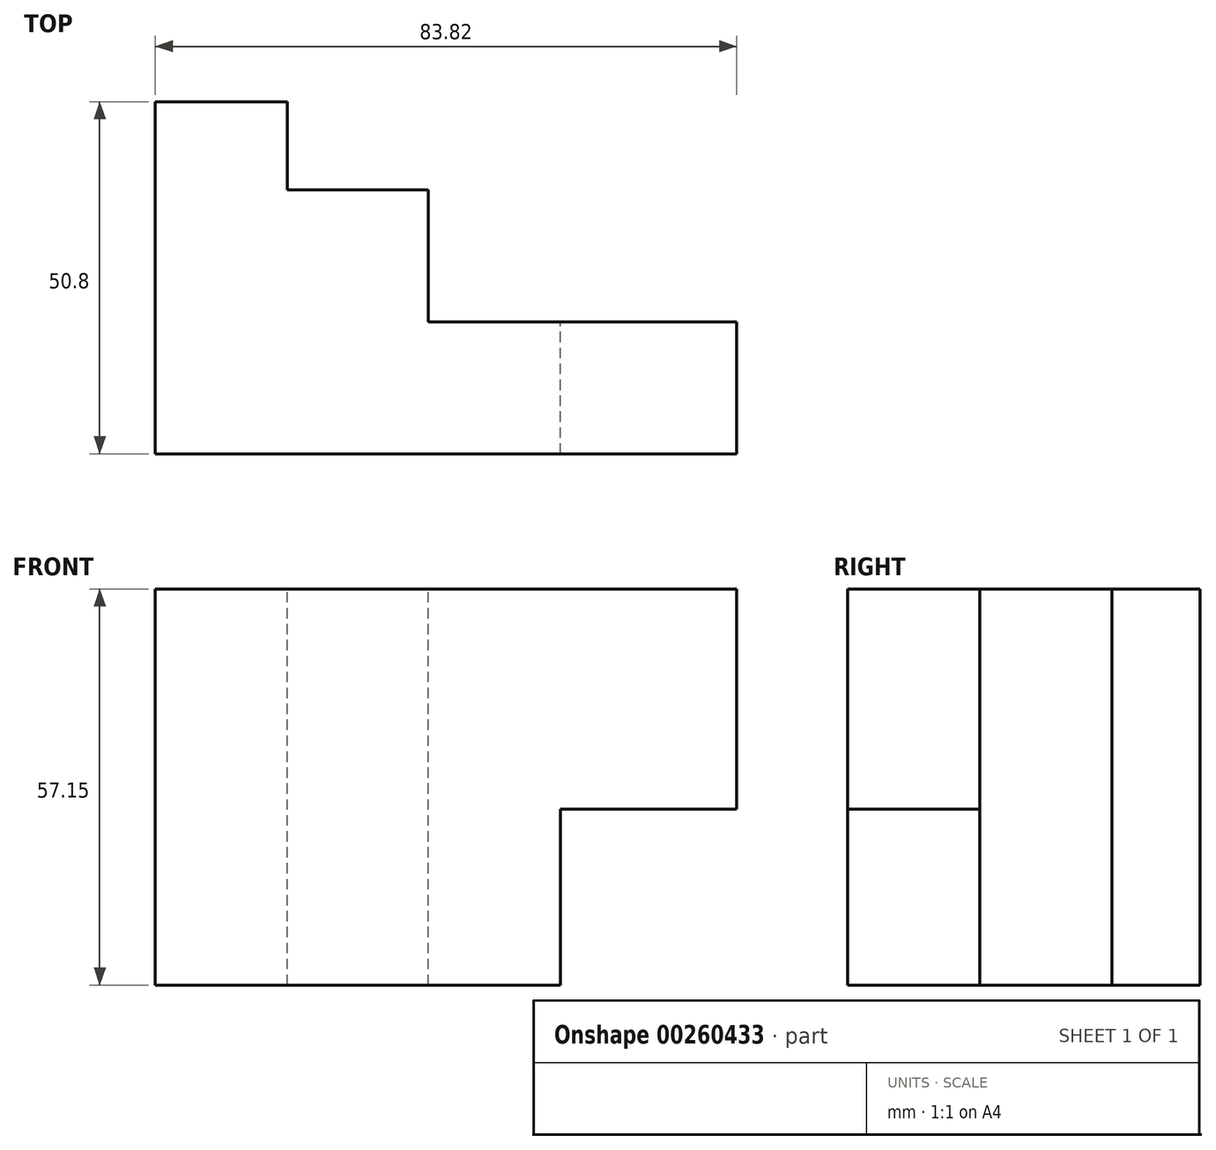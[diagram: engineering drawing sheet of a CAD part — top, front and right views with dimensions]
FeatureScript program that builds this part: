
annotation { "Feature Type Name" : "Feature", "Feature Type Description" : "" }
export const myFeature = defineFeature(function(context is Context, id is Id, definition is map)
    precondition{}
    {
        {
            var Q0;
            Q0=qCreatedBy(makeId("Top.planeOp"),FACE);
            var sketch = newSketch(context, id + "F0", { "sketchPlane" : qUnion([Q0])});
            skLineSegment(sketch, "E0", {"start": v(0, 0) * mm, "end": v(0, 50.8) * mm});
            skLineSegment(sketch, "E1", {"start": v(0, 50.8) * mm, "end": v(19.05, 50.8) * mm});
            skLineSegment(sketch, "E2", {"start": v(19.05, 50.8) * mm, "end": v(19.05, 38.1) * mm});
            skLineSegment(sketch, "E3", {"start": v(19.05, 38.1) * mm, "end": v(39.37, 38.1) * mm});
            skLineSegment(sketch, "E4", {"start": v(39.37, 38.1) * mm, "end": v(39.37, 19.05) * mm});
            skLineSegment(sketch, "E5", {"start": v(39.37, 19.05) * mm, "end": v(83.82, 19.05) * mm});
            skLineSegment(sketch, "E6", {"start": v(83.82, 19.05) * mm, "end": v(83.82, 0) * mm});
            skLineSegment(sketch, "E7", {"start": v(83.82, 0) * mm, "end": v(0, 0) * mm});
            skSolve(sketch);
        }
        {
            var Q0;
            Q0=makeQuery(id+"F0.imprint","IMPRINT",FACE,{"disambiguationData":[TD([[makeQuery(id+"F0.imprint","IMPRINT",EDGE,{"derivedFrom":sQuery(id+"F0.wireOp",EDGE,"E0")}),-1.0]])]});
            extrude(context, id + "F1", {"entities" : qUnion([Q0]), "oppositeDirection" : true, "depth" : 57.15 * mm});
        }
        {
            var Q0;
            Q0=makeQuery(id+"F1.opExtrude","SWEPT_FACE",FACE,{"disambiguationData":[OSD([sQuery(id+"F0.wireOp",EDGE,"E5")])]});
            var sketch = newSketch(context, id + "F2", { "sketchPlane" : qUnion([Q0])});
            skLineSegment(sketch, "E8.bottom", {"start": v(-83.82, -57.15) * mm, "end": v(-58.42, -57.15) * mm});
            skLineSegment(sketch, "E8.top", {"start": v(-83.82, -31.75) * mm, "end": v(-58.42, -31.75) * mm});
            skLineSegment(sketch, "E8.left", {"start": v(-83.82, -57.15) * mm, "end": v(-83.82, -31.75) * mm});
            skLineSegment(sketch, "E8.right", {"start": v(-58.42, -57.15) * mm, "end": v(-58.42, -31.75) * mm});
            skSolve(sketch);
        }
        {
            var Q0;
            Q0=makeQuery(id+"F2.imprint","IMPRINT",FACE,{"disambiguationData":[TD([[makeQuery(id+"F2.imprint","IMPRINT",EDGE,{"derivedFrom":sQuery(id+"F2.wireOp",EDGE,"E8.bottom")}),-1.0]])]});
            extrude(context, id + "F3", {"entities" : qUnion([Q0]), "operationType" : NewBodyOperationType.REMOVE, "endBound" : BoundingType.UP_TO_NEXT, "oppositeDirection" : true, "depth" : 25.4 * mm});
        }
    });
